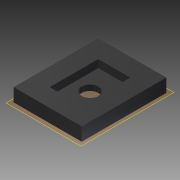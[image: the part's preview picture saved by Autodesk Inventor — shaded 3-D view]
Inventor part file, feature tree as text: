
AUTODESK INVENTOR PART (.ipt)
format: ipt  version: 2014 (Build 180170000, 170)  size: 107,520 bytes
history: native  units: mm
features: extrude x3, sketch x3, reference x2, plane x1
ambient origin geometry x8: Origin, YZ Plane, XZ Plane, XY Plane, X Axis, Y Axis, Z Axis, Center Point
bodies: Volumenkörper1 (feature_tree)
feature tree (9):
  plane  "Arbeitsebene1"
  extrude  "Extrusion1"  Depth=5.0mm
  extrude  "Extrusion2"  Depth=29.0mm
  extrude  "Extrusion4"  Depth=7.0mm TaperAngle=0.0deg
  sketch  "Skizze1"  dims[d0=5.0mm d1=0.0mm d2=15.0mm]
  reference  "Referenz1"
  reference  "Referenz2"
  sketch  "Skizze2"  dims[d3=5.0mm d4=0.0mm d9=29.0mm]
  sketch  "Skizze3"  dims[d10=44.0mm d11=7.0mm d12=0.0mm]
